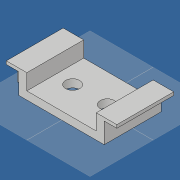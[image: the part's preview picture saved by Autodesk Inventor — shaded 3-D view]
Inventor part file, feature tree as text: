
AUTODESK INVENTOR PART (.ipt)
format: ipt  version: 2019 (Build 230136000, 136)  size: 111,616 bytes
history: native  units: mm
features: sketch x2, extrude x2, hole x1
ambient origin geometry x8: Origin, YZ Plane, XZ Plane, XY Plane, X Axis, Y Axis, Z Axis, Center Point
bodies: Volumenkörper1 (feature_tree)
feature tree (5):
  sketch  "Skizze1"  dims[d0=1.0mm d1=35.0mm]
  extrude  "Extrusion1"  Depth=35.0mm
  extrude  "Extrusion2"  Depth=7.5mm
  hole  "Bohrung1"  [1 undecoded]
  sketch  "Skizze2"  dims[d2=27.0mm d3=7.5mm d6=4.0mm d7=2.5mm d8=2.5mm d9=18.0mm d10=0.0mm d11=11.0mm d12=0.0mm d13=11.0mm d14=22.0mm d15=4.5mm d16=6.0mm d17=9.4mm d18=2.0mm d19=90.0deg d20=8.0mm d21=20.594885mm]
note: 1 required parameter value undecoded (feature->parameter linkage not recoverable at this tier; creation-order binding heuristic only, values carry confidence <= 0.55)
